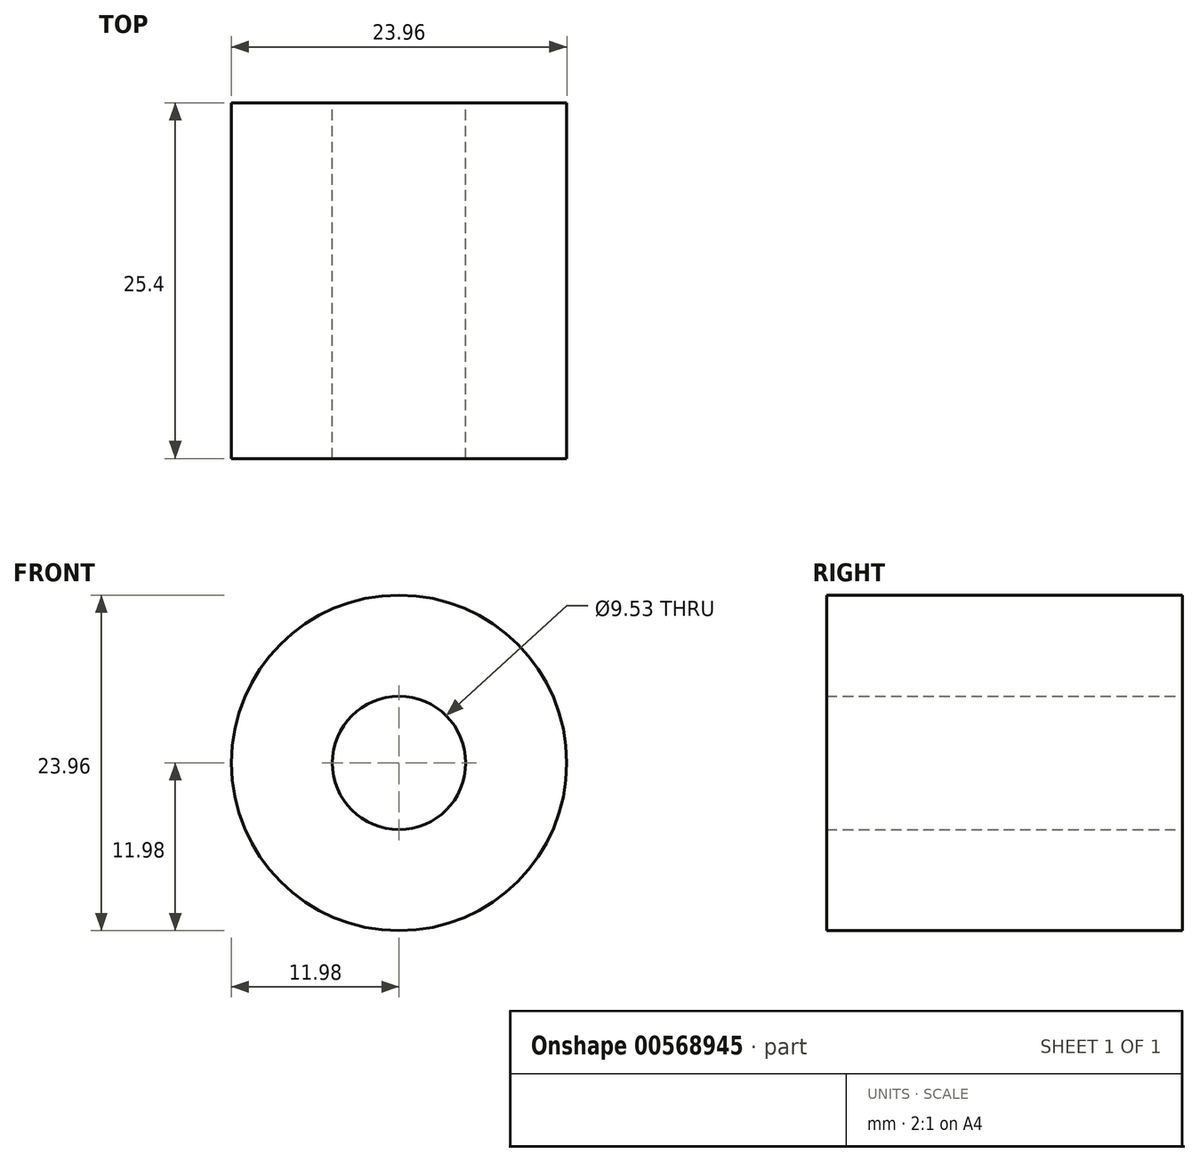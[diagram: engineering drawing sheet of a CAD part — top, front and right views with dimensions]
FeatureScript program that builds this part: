
annotation { "Feature Type Name" : "Feature", "Feature Type Description" : "" }
export const myFeature = defineFeature(function(context is Context, id is Id, definition is map)
    precondition{}
    {
        {
            var Q0;
            Q0=qCreatedBy(makeId("Front.planeOp"),FACE);
            var sketch = newSketch(context, id + "F0", { "sketchPlane" : qUnion([Q0])});
            skCircle(sketch, "E0", {"center": v(0, 0) * mm, "radius": 4.76 * mm});
            skCircle(sketch, "E1", {"center": v(0, 0) * mm, "radius": 11.98 * mm});
            skSolve(sketch);
        }
        {
            var Q0;
            Q0 = qSketchRegion(id + "F0", true);
            var Q1;
            Q1=makeQuery(id+"F0.imprint","IMPRINT",FACE,{"disambiguationData":[TD([[makeQuery(id+"F0.imprint","IMPRINT",EDGE,{"derivedFrom":sQuery(id+"F0.wireOp",EDGE,"E0")}),-1.0]])]});
            var Q2;
            Q2=makeQuery(id+"F0.imprint","IMPRINT",FACE,{"disambiguationData":[TD([[makeQuery(id+"F0.imprint","IMPRINT",EDGE,{"derivedFrom":sQuery(id+"F0.wireOp",EDGE,"3IE8iymb-vdL4-V3yI-AlVS-ZmHPS80ETRw6")}),-1.0]])]});
            extrude(context, id + "F1", {"entities" : qUnion([Q0, Q1, Q2]), "depth" : 25.4 * mm, "offsetDistance" : 25.4 * mm});
        }
    });
